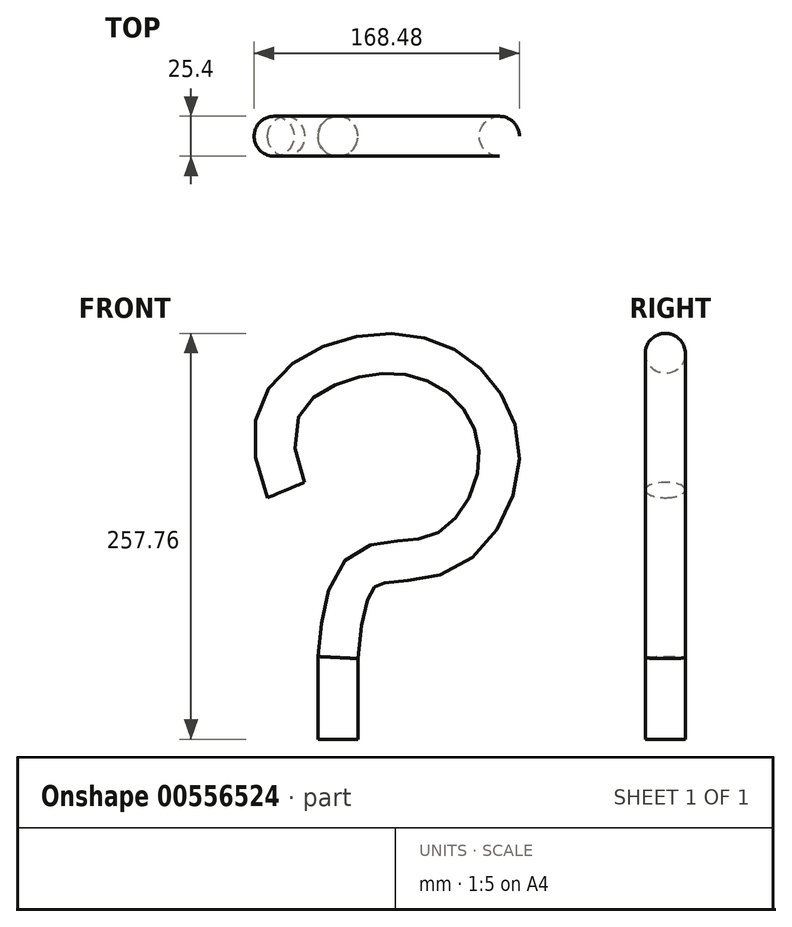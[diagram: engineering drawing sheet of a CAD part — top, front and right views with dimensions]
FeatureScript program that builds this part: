
annotation { "Feature Type Name" : "Feature", "Feature Type Description" : "" }
export const myFeature = defineFeature(function(context is Context, id is Id, definition is map)
    precondition{}
    {
        {
            var Q0;
            Q0=qCreatedBy(makeId("Top.planeOp"),FACE);
            var sketch = newSketch(context, id + "F0", { "sketchPlane" : qUnion([Q0])});
            skCircle(sketch, "E0", {"center": v(0, 0) * mm, "radius": 12.7 * mm});
            skSolve(sketch);
        }
        {
            var Q0;
            Q0=qCreatedBy(makeId("Front.planeOp"),FACE);
            var sketch = newSketch(context, id + "F1", { "sketchPlane" : qUnion([Q0])});
            skLineSegment(sketch, "E1", {"start": v(0, 0) * mm, "end": v(0, 51.87) * mm});
            skFitSpline(sketch, "E2", {"points": [v(0, 51.87) * mm, v(17.33, 108.05) * mm, v(65.74, 118.1) * mm, v(102.27, 173.8) * mm, v(82.18, 225.87) * mm, v(31.03, 245.05) * mm, v(-29.25, 221.3) * mm, v(-32.9, 158.28) * mm], "startDerivative": vector(51.46, 514.26) * mm, "endDerivative": vector(236.23, -563.13) * mm});
            skSolve(sketch);
        }
        {
            var Q0;
            Q0 = qSketchRegion(id + "F0", true);
            var Q1;
            Q1 = qConstructionFilter(qBodyType(qCreatedBy(id + "F1" ,EDGE), BodyType.WIRE), ConstructionObject.NO);
            sweep(context, id + "F2", {"profiles" : qUnion([Q0]), "path" : qUnion([Q1])});
        }
    });
